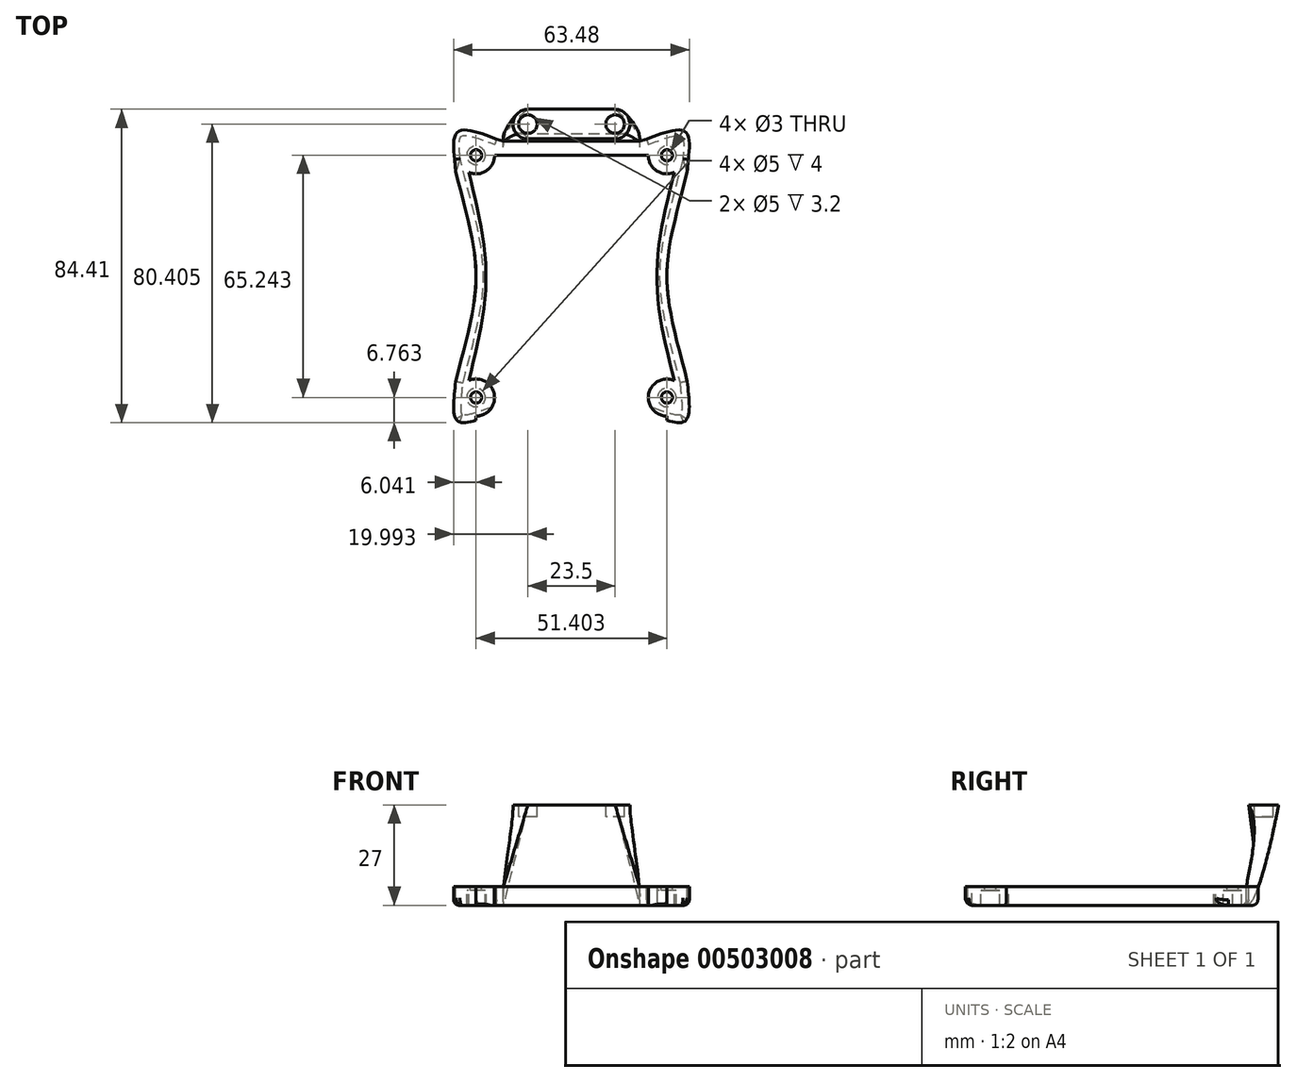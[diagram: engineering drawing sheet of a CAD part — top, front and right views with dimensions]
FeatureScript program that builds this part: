
annotation { "Feature Type Name" : "Feature", "Feature Type Description" : "" }
export const myFeature = defineFeature(function(context is Context, id is Id, definition is map)
    precondition{}
    {
        {
            var Q0;
            Q0=qCreatedBy(makeId("Top.planeOp"),FACE);
            var sketch = newSketch(context, id + "F0", { "sketchPlane" : qUnion([Q0])});
            skPoint(sketch, "E0.middle", {"position": v(-2.33, 0.15) * mm});
            skLineSegment(sketch, "E1.bottom", {"start": v(23.37, 32.78) * mm, "end": v(-28.03, 32.78) * mm, "construction": true});
            skLineSegment(sketch, "E1.top", {"start": v(23.37, -32.47) * mm, "end": v(-28.03, -32.47) * mm, "construction": true});
            skLineSegment(sketch, "E1.left", {"start": v(23.37, 32.78) * mm, "end": v(23.37, -32.47) * mm, "construction": true});
            skLineSegment(sketch, "E1.right", {"start": v(-28.03, 32.78) * mm, "end": v(-28.03, -32.47) * mm, "construction": true});
            skLineSegment(sketch, "E2.bottom", {"start": v(-67.33, 82.65) * mm, "end": v(62.67, 82.65) * mm, "construction": true});
            skLineSegment(sketch, "E2.top", {"start": v(-67.33, -82.35) * mm, "end": v(62.67, -82.35) * mm, "construction": true});
            skLineSegment(sketch, "E2.left", {"start": v(-67.33, 82.65) * mm, "end": v(-67.33, -82.35) * mm, "construction": true});
            skLineSegment(sketch, "E2.right", {"start": v(62.67, 82.65) * mm, "end": v(62.67, -82.35) * mm, "construction": true});
            skCircle(sketch, "E3", {"center": v(62.67, 82.65) * mm, "radius": 4.5 * mm, "construction": true});
            skCircle(sketch, "E4", {"center": v(-67.33, 82.65) * mm, "radius": 4.5 * mm, "construction": true});
            skCircle(sketch, "E5", {"center": v(62.67, -82.35) * mm, "radius": 4.5 * mm, "construction": true});
            skCircle(sketch, "E6", {"center": v(-67.33, -82.35) * mm, "radius": 4.5 * mm, "construction": true});
            skCircle(sketch, "E7", {"center": v(62.67, 82.65) * mm, "radius": 8 * mm, "construction": true});
            skCircle(sketch, "E8", {"center": v(62.67, -82.35) * mm, "radius": 8 * mm, "construction": true});
            skCircle(sketch, "E9", {"center": v(-67.33, -82.35) * mm, "radius": 8 * mm, "construction": true});
            skCircle(sketch, "E10", {"center": v(-67.33, 82.65) * mm, "radius": 8 * mm, "construction": true});
            skCircle(sketch, "E11", {"center": v(62.67, 82.65) * mm, "radius": 9.5 * mm, "construction": true});
            skCircle(sketch, "E12", {"center": v(62.67, -82.35) * mm, "radius": 9.5 * mm, "construction": true});
            skCircle(sketch, "E13", {"center": v(-67.33, -82.35) * mm, "radius": 9.5 * mm, "construction": true});
            skCircle(sketch, "E14", {"center": v(-67.33, 82.65) * mm, "radius": 9.5 * mm, "construction": true});
            skCircle(sketch, "E15", {"center": v(62.67, 82.65) * mm, "radius": 14 * mm, "construction": true});
            skCircle(sketch, "E16", {"center": v(-67.33, 82.65) * mm, "radius": 14 * mm, "construction": true});
            skCircle(sketch, "E17", {"center": v(62.67, -82.35) * mm, "radius": 14 * mm, "construction": true});
            skCircle(sketch, "E18", {"center": v(-67.33, -82.35) * mm, "radius": 14 * mm, "construction": true});
            skCircle(sketch, "E19", {"center": v(62.67, 82.65) * mm, "radius": 63.5 * mm, "construction": true});
            skCircle(sketch, "E20", {"center": v(62.67, -82.35) * mm, "radius": 63.5 * mm, "construction": true});
            skCircle(sketch, "E21", {"center": v(-67.33, -82.35) * mm, "radius": 63.5 * mm, "construction": true});
            skCircle(sketch, "E22", {"center": v(-67.33, 82.65) * mm, "radius": 63.5 * mm, "construction": true});
            skLineSegment(sketch, "E23.bottom", {"start": v(-28.52, 26.34) * mm, "end": v(23.86, 26.34) * mm, "construction": true});
            skLineSegment(sketch, "E23.top", {"start": v(-28.52, -26.04) * mm, "end": v(23.86, -26.04) * mm, "construction": true});
            skLineSegment(sketch, "E23.left", {"start": v(-28.52, 26.34) * mm, "end": v(-28.52, -26.04) * mm, "construction": true});
            skLineSegment(sketch, "E23.right", {"start": v(23.86, 26.34) * mm, "end": v(23.86, -26.04) * mm, "construction": true});
            skCircle(sketch, "E24", {"center": v(23.37, 32.78) * mm, "radius": 1.5 * mm, "construction": true});
            skCircle(sketch, "E25", {"center": v(-28.03, 32.78) * mm, "radius": 1.5 * mm, "construction": true});
            skCircle(sketch, "E26", {"center": v(23.37, -32.47) * mm, "radius": 1.5 * mm, "construction": true});
            skCircle(sketch, "E27", {"center": v(-28.03, -32.47) * mm, "radius": 1.5 * mm, "construction": true});
            skLineSegment(sketch, "E28", {"start": v(-67.33, 82.65) * mm, "end": v(62.67, -82.35) * mm, "construction": true});
            skLineSegment(sketch, "E29", {"start": v(62.67, 82.65) * mm, "end": v(-67.33, -82.35) * mm, "construction": true});
            skLineSegment(sketch, "E30.bottom", {"start": v(-17.58, -3.46) * mm, "end": v(12.92, -3.46) * mm, "construction": true});
            skLineSegment(sketch, "E30.top", {"start": v(-17.58, -33.96) * mm, "end": v(12.92, -33.96) * mm, "construction": true});
            skLineSegment(sketch, "E30.left", {"start": v(-17.58, -3.46) * mm, "end": v(-17.58, -33.96) * mm, "construction": true});
            skLineSegment(sketch, "E30.right", {"start": v(12.92, -3.46) * mm, "end": v(12.92, -33.96) * mm, "construction": true});
            skPoint(sketch, "E30.middle", {"position": v(-2.33, -18.71) * mm});
            skLineSegment(sketch, "E31.bottom", {"start": v(-17.58, 33.04) * mm, "end": v(12.92, 33.04) * mm, "construction": true});
            skLineSegment(sketch, "E31.top", {"start": v(-17.58, 2.54) * mm, "end": v(12.92, 2.54) * mm, "construction": true});
            skLineSegment(sketch, "E31.left", {"start": v(-17.58, 33.04) * mm, "end": v(-17.58, 2.54) * mm, "construction": true});
            skLineSegment(sketch, "E31.right", {"start": v(12.92, 33.04) * mm, "end": v(12.92, 2.54) * mm, "construction": true});
            skPoint(sketch, "E31.middle", {"position": v(-2.33, 17.79) * mm});
            skLineSegment(sketch, "E32", {"start": v(-2.33, 2.54) * mm, "end": v(-2.33, -3.46) * mm, "construction": true});
            skLineSegment(sketch, "E33", {"start": v(-2.33, 41.17) * mm, "end": v(-14.08, 41.17) * mm, "construction": true});
            skLineSegment(sketch, "E34", {"start": v(-2.33, 41.17) * mm, "end": v(9.42, 41.17) * mm, "construction": true});
            skLineSegment(sketch, "E35", {"start": v(-28.03, 32.78) * mm, "end": v(-22.53, 37.1) * mm, "construction": true});
            skLineSegment(sketch, "E36", {"start": v(-28.03, 32.78) * mm, "end": v(-33.53, 28.44) * mm, "construction": true});
            skLineSegment(sketch, "E37", {"start": v(-28.03, 32.78) * mm, "end": v(-32.98, 39.06) * mm, "construction": true});
            skLineSegment(sketch, "E38", {"start": v(23.37, 32.78) * mm, "end": v(28.33, 39.06) * mm, "construction": true});
            skLineSegment(sketch, "E39", {"start": v(23.37, 32.78) * mm, "end": v(17.88, 37.1) * mm, "construction": true});
            skLineSegment(sketch, "E40", {"start": v(23.37, 32.78) * mm, "end": v(28.87, 28.44) * mm, "construction": true});
            skLineSegment(sketch, "E41", {"start": v(23.37, -32.47) * mm, "end": v(28.33, -38.75) * mm, "construction": true});
            skLineSegment(sketch, "E42", {"start": v(23.37, -32.47) * mm, "end": v(17.88, -36.8) * mm, "construction": true});
            skLineSegment(sketch, "E43", {"start": v(23.37, -32.47) * mm, "end": v(28.87, -28.13) * mm, "construction": true});
            skLineSegment(sketch, "E44", {"start": v(-28.03, -32.47) * mm, "end": v(-32.98, -38.75) * mm, "construction": true});
            skLineSegment(sketch, "E45", {"start": v(-28.03, -32.47) * mm, "end": v(-22.53, -36.8) * mm, "construction": true});
            skLineSegment(sketch, "E46", {"start": v(-28.03, -32.47) * mm, "end": v(-33.53, -28.13) * mm, "construction": true});
            skFitSpline(sketch, "E47", {"points": [v(-22.53, 37.1) * mm, v(-32.98, 39.06) * mm, v(-33.53, 28.44) * mm], "startDerivative": vector(-20.3, 7.46) * mm, "endDerivative": vector(0.93, -21.61) * mm});
            skFitSpline(sketch, "E48", {"points": [v(17.88, 37.1) * mm, v(28.33, 39.06) * mm, v(28.87, 28.44) * mm], "startDerivative": vector(20.3, 7.46) * mm, "endDerivative": vector(-0.93, -21.61) * mm});
            skLineSegment(sketch, "E49", {"start": v(-14.08, 41.17) * mm, "end": v(-18.08, 41.17) * mm, "construction": true});
            skLineSegment(sketch, "E50", {"start": v(9.42, 41.17) * mm, "end": v(13.42, 41.17) * mm, "construction": true});
            skLineSegment(sketch, "E51", {"start": v(-2.33, 41.17) * mm, "end": v(-2.33, 45.17) * mm, "construction": true});
            skLineSegment(sketch, "E52", {"start": v(-18.08, 41.17) * mm, "end": v(-18.08, 41.17) * mm});
            skLineSegment(sketch, "E53", {"start": v(13.42, 41.17) * mm, "end": v(13.42, 41.17) * mm});
            skPoint(sketch, "E54.visualSharp", {"position": v(-18.08, 45.17) * mm});
            skPoint(sketch, "E55.visualSharp", {"position": v(13.42, 45.17) * mm});
            skLineSegment(sketch, "E56", {"start": v(-22.53, 37.1) * mm, "end": v(-20.66, 36.53) * mm});
            skPoint(sketch, "E57.visualSharp", {"position": v(-18.08, 35.74) * mm});
            skLineSegment(sketch, "E58", {"start": v(-18.08, 35.74) * mm, "end": v(-2.33, 35.74) * mm, "construction": true});
            skLineSegment(sketch, "E59", {"start": v(-2.33, 35.74) * mm, "end": v(13.42, 35.74) * mm, "construction": true});
            skLineSegment(sketch, "E60", {"start": v(17.88, 37.1) * mm, "end": v(16.01, 36.53) * mm});
            skPoint(sketch, "E61.visualSharp", {"position": v(13.42, 35.74) * mm});
            skCircle(sketch, "E62", {"center": v(-17.58, -33.96) * mm, "radius": 1.5 * mm});
            skCircle(sketch, "E63", {"center": v(12.92, -33.96) * mm, "radius": 1.5 * mm});
            skLineSegment(sketch, "E64", {"start": v(-2.33, -33.96) * mm, "end": v(-2.33, -37.96) * mm, "construction": true});
            skLineSegment(sketch, "E65", {"start": v(-17.58, -33.96) * mm, "end": v(-21.58, -33.96) * mm, "construction": true});
            skLineSegment(sketch, "E66", {"start": v(12.92, -33.96) * mm, "end": v(16.92, -33.96) * mm, "construction": true});
            skLineSegment(sketch, "E67", {"start": v(-21.58, -38.3) * mm, "end": v(-2.33, -38.3) * mm, "construction": true});
            skLineSegment(sketch, "E68", {"start": v(-2.33, -38.3) * mm, "end": v(16.92, -38.3) * mm, "construction": true});
            skPoint(sketch, "E69.visualSharp", {"position": v(-21.58, -38.3) * mm});
            skPoint(sketch, "E70.visualSharp", {"position": v(16.92, -38.3) * mm});
            skCircle(sketch, "E71", {"center": v(-12.13, -44.75) * mm, "radius": 1.5 * mm});
            skCircle(sketch, "E72", {"center": v(7.47, -44.75) * mm, "radius": 1.5 * mm});
            skLineSegment(sketch, "E73", {"start": v(-12.13, -44.75) * mm, "end": v(-2.33, -44.75) * mm, "construction": true});
            skLineSegment(sketch, "E74", {"start": v(-2.33, -44.75) * mm, "end": v(7.47, -44.75) * mm, "construction": true});
            skFitSpline(sketch, "E75", {"points": [v(-33.53, 28.44) * mm, v(-28.03, 0.15) * mm, v(-33.53, -28.13) * mm], "startDerivative": vector(16.96, -67.18) * mm, "endDerivative": vector(-16.96, -67.18) * mm});
            skFitSpline(sketch, "E76", {"points": [v(28.87, 28.44) * mm, v(23.37, 0.15) * mm, v(28.87, -28.13) * mm], "startDerivative": vector(-16.96, -67.18) * mm, "endDerivative": vector(16.96, -67.18) * mm});
            skLineSegment(sketch, "E77", {"start": v(-2.33, -44.75) * mm, "end": v(-2.33, -50.75) * mm, "construction": true});
            skLineSegment(sketch, "E78", {"start": v(-12.13, -44.75) * mm, "end": v(-16.13, -44.75) * mm, "construction": true});
            skLineSegment(sketch, "E79", {"start": v(-12.13, -44.75) * mm, "end": v(-12.13, -48.75) * mm, "construction": true});
            skLineSegment(sketch, "E80", {"start": v(7.47, -44.75) * mm, "end": v(11.47, -44.75) * mm, "construction": true});
            skLineSegment(sketch, "E81", {"start": v(7.47, -44.75) * mm, "end": v(7.47, -48.75) * mm, "construction": true});
            skCircle(sketch, "E82", {"center": v(-28.03, 32.78) * mm, "radius": 1.5 * mm});
            skCircle(sketch, "E83", {"center": v(23.37, 32.78) * mm, "radius": 1.5 * mm});
            skCircle(sketch, "E84", {"center": v(-28.03, -32.47) * mm, "radius": 1.5 * mm});
            skCircle(sketch, "E85", {"center": v(23.37, -32.47) * mm, "radius": 1.5 * mm});
            skLineSegment(sketch, "E86", {"start": v(-2.33, 32.78) * mm, "end": v(-2.33, 41.17) * mm, "construction": true});
            skLineSegment(sketch, "E87", {"start": v(115.22, -24.48) * mm, "end": v(115.22, 9.49) * mm, "construction": true});
            skLineSegment(sketch, "E88", {"start": v(-21.37, -36.36) * mm, "end": v(-2.33, -36.36) * mm, "construction": true});
            skLineSegment(sketch, "E89", {"start": v(-2.33, -36.36) * mm, "end": v(16.72, -36.36) * mm, "construction": true});
            skFitSpline(sketch, "E90", {"points": [v(-21.58, -38.3) * mm, v(-16.13, -44.75) * mm, v(-12.13, -48.75) * mm, v(-2.33, -50.75) * mm], "startDerivative": vector(17.01, -18.5) * mm, "endDerivative": vector(29.8, -3.11) * mm});
            skFitSpline(sketch, "E91", {"points": [v(16.92, -38.3) * mm, v(11.47, -44.75) * mm, v(7.47, -48.75) * mm, v(-2.33, -50.75) * mm], "startDerivative": vector(-17.98, -19.6) * mm, "endDerivative": vector(-29.8, -3.11) * mm});
            skLineSegment(sketch, "E92", {"start": v(116.25, 10.49) * mm, "end": v(169.47, 8.84) * mm, "construction": true});
            skPoint(sketch, "E93.visualSharp", {"position": v(115.22, 10.52) * mm});
            skArc(sketch, "E93.filletArc", {"start": v(116.25, 10.49) * mm, "mid": v(115.53, 10.2) * mm, "end": v(115.22, 9.49) * mm, "construction": true});
            skPoint(sketch, "E94.visualSharp", {"position": v(16.72, -36.36) * mm});
            skPoint(sketch, "E95.visualSharp", {"position": v(-21.37, -36.36) * mm});
            skLineSegment(sketch, "E96.bottom", {"start": v(-16.1, 17.65) * mm, "end": v(11.45, 17.65) * mm, "construction": true});
            skLineSegment(sketch, "E96.top", {"start": v(-16.1, -17.35) * mm, "end": v(11.45, -17.35) * mm, "construction": true});
            skLineSegment(sketch, "E96.left", {"start": v(-16.1, 17.65) * mm, "end": v(-16.1, -17.35) * mm, "construction": true});
            skLineSegment(sketch, "E96.right", {"start": v(11.45, 17.65) * mm, "end": v(11.45, -17.35) * mm, "construction": true});
            skLineSegment(sketch, "E97", {"start": v(-2.33, 13.23) * mm, "end": v(-20.53, 13.23) * mm, "construction": true});
            skLineSegment(sketch, "E98", {"start": v(-2.33, 13.23) * mm, "end": v(15.88, 13.23) * mm, "construction": true});
            skLineSegment(sketch, "E99", {"start": v(-2.33, 0.15) * mm, "end": v(-2.33, 14.42) * mm, "construction": true});
            skLineSegment(sketch, "E100", {"start": v(-2.33, 0.15) * mm, "end": v(14.67, 0.15) * mm, "construction": true});
            skLineSegment(sketch, "E101.bottom", {"start": v(-18.22, 14.7) * mm, "end": v(13.57, 14.7) * mm, "construction": true});
            skLineSegment(sketch, "E101.top", {"start": v(-18.22, -14.4) * mm, "end": v(13.57, -14.4) * mm, "construction": true});
            skLineSegment(sketch, "E101.left", {"start": v(-18.22, 14.7) * mm, "end": v(-18.22, -14.4) * mm, "construction": true});
            skLineSegment(sketch, "E101.right", {"start": v(13.57, 14.7) * mm, "end": v(13.57, -14.4) * mm, "construction": true});
            skLineSegment(sketch, "E102", {"start": v(-2.33, 26.07) * mm, "end": v(12, 26.07) * mm, "construction": true});
            skLineSegment(sketch, "E103", {"start": v(-2.33, 26.07) * mm, "end": v(-16.66, 26.07) * mm, "construction": true});
            skLineSegment(sketch, "E104.top", {"start": v(-17.4, 22.07) * mm, "end": v(-15.9, 22.07) * mm});
            skPoint(sketch, "E104.middle", {"position": v(-16.66, 26.07) * mm});
            skLineSegment(sketch, "E105.top", {"start": v(12.75, 22.07) * mm, "end": v(11.25, 22.07) * mm});
            skLineSegment(sketch, "E105.left", {"start": v(12.75, 30.07) * mm, "end": v(12.75, 22.07) * mm});
            skPoint(sketch, "E105.middle", {"position": v(12, 26.07) * mm});
            skFitSpline(sketch, "E106", {"points": [v(-33.53, -28.13) * mm, v(-32.98, -38.75) * mm, v(-22.93, -36.94) * mm], "startDerivative": vector(-1.92, -24.87) * mm, "endDerivative": vector(23.17, 7.34) * mm});
            skLineSegment(sketch, "E107", {"start": v(-22.93, -36.94) * mm, "end": v(-2.33, -36.94) * mm, "construction": true});
            skLineSegment(sketch, "E108", {"start": v(-2.33, -36.94) * mm, "end": v(18.28, -36.94) * mm, "construction": true});
            skLineSegment(sketch, "E109", {"start": v(16.92, -38.3) * mm, "end": v(17.66, -37.14) * mm});
            skLineSegment(sketch, "E110", {"start": v(18.25, -36.93) * mm, "end": v(18.28, -36.94) * mm});
            skLineSegment(sketch, "E111", {"start": v(-21.58, -38.3) * mm, "end": v(-22.32, -37.14) * mm});
            skLineSegment(sketch, "E112", {"start": v(-22.9, -36.93) * mm, "end": v(-22.93, -36.94) * mm});
            skLineSegment(sketch, "E113", {"start": v(169.47, 8.84) * mm, "end": v(169.47, -13.62) * mm, "construction": true});
            skPoint(sketch, "E114.visualSharp", {"position": v(17.88, -36.8) * mm});
            skArc(sketch, "E114.filletArc", {"start": v(18.25, -36.93) * mm, "mid": v(17.92, -36.93) * mm, "end": v(17.66, -37.14) * mm});
            skPoint(sketch, "E115.visualSharp", {"position": v(-22.53, -36.8) * mm});
            skArc(sketch, "E115.filletArc", {"start": v(-22.32, -37.14) * mm, "mid": v(-22.58, -36.93) * mm, "end": v(-22.9, -36.93) * mm});
            skLineSegment(sketch, "E116", {"start": v(-2.33, 0.15) * mm, "end": v(-2.33, 3.45) * mm, "construction": true});
            skLineSegment(sketch, "E117.bottom", {"start": v(-7.83, 5.65) * mm, "end": v(3.17, 5.65) * mm, "construction": true});
            skLineSegment(sketch, "E117.top", {"start": v(-7.83, -5.35) * mm, "end": v(3.17, -5.35) * mm, "construction": true});
            skLineSegment(sketch, "E117.left", {"start": v(-7.83, 5.65) * mm, "end": v(-7.83, -5.35) * mm, "construction": true});
            skLineSegment(sketch, "E117.right", {"start": v(3.17, 5.65) * mm, "end": v(3.17, -5.35) * mm, "construction": true});
            skLineSegment(sketch, "E118.bottom", {"start": v(-10.3, 10.77) * mm, "end": v(5.65, 10.77) * mm});
            skPoint(sketch, "E118.middle", {"position": v(-2.33, 12.75) * mm});
            skPoint(sketch, "E119.middle", {"position": v(-2.33, -26.45) * mm});
            skPoint(sketch, "E120", {"position": v(-2.33, -17.35) * mm});
            skPoint(sketch, "E121", {"position": v(-2.33, -26.04) * mm});
            skPoint(sketch, "E122.visualSharp", {"position": v(-2.33, 21.17) * mm});
            skArc(sketch, "E122.filletArc", {"start": v(-0.91, 19.76) * mm, "mid": v(-2.33, 20.34) * mm, "end": v(-3.74, 19.76) * mm});
            skPoint(sketch, "E123.visualSharp", {"position": v(-12.72, 10.77) * mm});
            skArc(sketch, "E123.filletArc", {"start": v(-11.02, 12.48) * mm, "mid": v(-11.23, 11.4) * mm, "end": v(-10.3, 10.77) * mm});
            skPoint(sketch, "E124.visualSharp", {"position": v(8.07, 10.77) * mm});
            skArc(sketch, "E124.filletArc", {"start": v(5.65, 10.77) * mm, "mid": v(6.58, 11.4) * mm, "end": v(6.36, 12.48) * mm});
            skPoint(sketch, "E125.visualSharp", {"position": v(-2.33, 0.75) * mm});
            skLineSegment(sketch, "E126", {"start": v(-1.33, 10.77) * mm, "end": v(-1.33, 6.27) * mm, "construction": true});
            skPoint(sketch, "E127.middle", {"position": v(-2.33, 9.75) * mm});
            skCircle(sketch, "E128", {"center": v(13.57, 14.7) * mm, "radius": 4.5 * mm, "construction": true});
            skCircle(sketch, "E129", {"center": v(-18.22, 14.7) * mm, "radius": 4.5 * mm, "construction": true});
            skCircle(sketch, "E130", {"center": v(13.57, -14.4) * mm, "radius": 4.5 * mm, "construction": true});
            skCircle(sketch, "E131", {"center": v(-18.22, -14.4) * mm, "radius": 4.5 * mm, "construction": true});
            skLineSegment(sketch, "E132", {"start": v(-2.33, 0.15) * mm, "end": v(-18.22, 14.7) * mm, "construction": true});
            skLineSegment(sketch, "E133", {"start": v(-2.33, 0.15) * mm, "end": v(13.57, 14.7) * mm, "construction": true});
            skLineSegment(sketch, "E134", {"start": v(13.57, 14.7) * mm, "end": v(23.37, 32.78) * mm, "construction": true});
            skLineSegment(sketch, "E135", {"start": v(-18.22, 14.7) * mm, "end": v(-28.03, 32.78) * mm, "construction": true});
            skLineSegment(sketch, "E136", {"start": v(-2.33, 0.15) * mm, "end": v(-18.22, -14.4) * mm, "construction": true});
            skLineSegment(sketch, "E137", {"start": v(-18.22, -14.4) * mm, "end": v(-28.03, -32.47) * mm, "construction": true});
            skLineSegment(sketch, "E138", {"start": v(-2.33, 0.15) * mm, "end": v(13.57, -14.4) * mm, "construction": true});
            skLineSegment(sketch, "E139", {"start": v(13.57, -14.4) * mm, "end": v(23.37, -32.47) * mm, "construction": true});
            skPoint(sketch, "E140.visualSharp", {"position": v(-4.57, 37.81) * mm});
            skPoint(sketch, "E141.visualSharp", {"position": v(-12.93, 29.46) * mm});
            skPoint(sketch, "E142.visualSharp", {"position": v(-4.57, 26.22) * mm});
            skArc(sketch, "E142.filletArc", {"start": v(-5.16, 25.63) * mm, "mid": v(-4.73, 26.28) * mm, "end": v(-4.57, 27.04) * mm});
            skPoint(sketch, "E143.visualSharp", {"position": v(-0.08, 26.22) * mm});
            skPoint(sketch, "E144.visualSharp", {"position": v(-0.08, 37.81) * mm});
            skPoint(sketch, "E145.visualSharp", {"position": v(8.28, 17.86) * mm});
            skPoint(sketch, "E146.visualSharp", {"position": v(-12.93, 17.86) * mm});
            skLineSegment(sketch, "E147", {"start": v(-2.33, -22.87) * mm, "end": v(-10.31, -22.87) * mm});
            skLineSegment(sketch, "E148", {"start": v(-2.33, -22.87) * mm, "end": v(5.66, -22.87) * mm});
            skPoint(sketch, "E149.visualSharp", {"position": v(8.07, -22.87) * mm});
            skArc(sketch, "E149.filletArc", {"start": v(6.37, -24.57) * mm, "mid": v(6.58, -23.48) * mm, "end": v(5.66, -22.87) * mm});
            skPoint(sketch, "E150.visualSharp", {"position": v(-12.73, -22.87) * mm});
            skArc(sketch, "E150.filletArc", {"start": v(-10.31, -22.87) * mm, "mid": v(-11.24, -23.48) * mm, "end": v(-11.02, -24.57) * mm});
            skPoint(sketch, "E151.visualSharp", {"position": v(-2.33, -33.27) * mm});
            skArc(sketch, "E151.filletArc", {"start": v(-3.74, -31.85) * mm, "mid": v(-2.33, -32.44) * mm, "end": v(-0.91, -31.85) * mm});
            skFitSpline(sketch, "E152", {"points": [v(28.87, -28.13) * mm, v(28.33, -38.75) * mm, v(18.28, -36.94) * mm], "startDerivative": vector(1.93, -24.89) * mm, "endDerivative": vector(-23.2, 7.39) * mm});
            skLineSegment(sketch, "E153", {"start": v(-5.66, -36.7) * mm, "end": v(-5.66, -42.34) * mm});
            skLineSegment(sketch, "E154", {"start": v(-12.73, -36.85) * mm, "end": v(-12.73, -31.22) * mm});
            skLineSegment(sketch, "E155", {"start": v(1, -36.7) * mm, "end": v(1, -42.34) * mm});
            skLineSegment(sketch, "E156", {"start": v(8.07, -36.85) * mm, "end": v(8.07, -31.22) * mm});
            skPoint(sketch, "E157.visualSharp", {"position": v(8.07, -28.8) * mm});
            skArc(sketch, "E157.filletArc", {"start": v(8.07, -31.22) * mm, "mid": v(7.46, -30.3) * mm, "end": v(6.37, -30.5) * mm});
            skPoint(sketch, "E158.visualSharp", {"position": v(1, -44.75) * mm});
            skArc(sketch, "E158.filletArc", {"start": v(1, -42.34) * mm, "mid": v(1.62, -43.26) * mm, "end": v(2.7, -43.05) * mm});
            skPoint(sketch, "E159.visualSharp", {"position": v(-5.66, -44.75) * mm});
            skArc(sketch, "E159.filletArc", {"start": v(-7.36, -43.05) * mm, "mid": v(-6.27, -43.26) * mm, "end": v(-5.66, -42.34) * mm});
            skPoint(sketch, "E160.visualSharp", {"position": v(-12.73, -28.8) * mm});
            skArc(sketch, "E160.filletArc", {"start": v(-11.02, -30.5) * mm, "mid": v(-12.1, -30.3) * mm, "end": v(-12.73, -31.22) * mm});
            skPoint(sketch, "E161.visualSharp", {"position": v(-5.66, -35.87) * mm});
            skArc(sketch, "E161.filletArc", {"start": v(-5.66, -36.7) * mm, "mid": v(-5.8, -35.94) * mm, "end": v(-6.24, -35.29) * mm});
            skPoint(sketch, "E162.visualSharp", {"position": v(-12.73, -37.68) * mm});
            skArc(sketch, "E162.filletArc", {"start": v(-12.73, -36.85) * mm, "mid": v(-12.57, -37.62) * mm, "end": v(-12.14, -38.27) * mm});
            skPoint(sketch, "E163.visualSharp", {"position": v(1, -35.87) * mm});
            skArc(sketch, "E163.filletArc", {"start": v(1.59, -35.29) * mm, "mid": v(1.15, -35.94) * mm, "end": v(1, -36.7) * mm});
            skPoint(sketch, "E164.visualSharp", {"position": v(8.07, -37.68) * mm});
            skArc(sketch, "E164.filletArc", {"start": v(7.49, -38.27) * mm, "mid": v(7.92, -37.62) * mm, "end": v(8.07, -36.85) * mm});
            skLineSegment(sketch, "E165", {"start": v(-2.33, -18.71) * mm, "end": v(-10.31, -18.71) * mm});
            skLineSegment(sketch, "E166", {"start": v(-2.33, -18.71) * mm, "end": v(5.66, -18.71) * mm});
            skPoint(sketch, "E167.visualSharp", {"position": v(-2.33, -8.31) * mm});
            skArc(sketch, "E167.filletArc", {"start": v(-0.91, -9.72) * mm, "mid": v(-2.33, -9.14) * mm, "end": v(-3.74, -9.72) * mm});
            skPoint(sketch, "E168.visualSharp", {"position": v(-12.73, -18.71) * mm});
            skArc(sketch, "E168.filletArc", {"start": v(-11.02, -17) * mm, "mid": v(-11.24, -18.1) * mm, "end": v(-10.31, -18.71) * mm});
            skPoint(sketch, "E169.visualSharp", {"position": v(8.07, -18.71) * mm});
            skArc(sketch, "E169.filletArc", {"start": v(5.66, -18.71) * mm, "mid": v(6.58, -18.1) * mm, "end": v(6.37, -17) * mm});
            skLineSegment(sketch, "E170", {"start": v(14.67, 0.15) * mm, "end": v(17.67, 0.15) * mm, "construction": true});
            skCircle(sketch, "E171", {"center": v(23.37, 32.78) * mm, "radius": 7 * mm, "construction": true});
            skLineSegment(sketch, "E172", {"start": v(17.64, 12.88) * mm, "end": v(21.69, 20.22) * mm});
            skLineSegment(sketch, "E173", {"start": v(16.8, 5.92) * mm, "end": v(12.23, 5.92) * mm});
            skPoint(sketch, "E174.visualSharp", {"position": v(22.7, 22.04) * mm});
            skArc(sketch, "E174.filletArc", {"start": v(22.15, 20.04) * mm, "mid": v(22, 20.33) * mm, "end": v(21.69, 20.22) * mm});
            skPoint(sketch, "E175.visualSharp", {"position": v(18.33, 5.92) * mm});
            skArc(sketch, "E175.filletArc", {"start": v(16.8, 5.92) * mm, "mid": v(18.02, 6.34) * mm, "end": v(18.73, 7.4) * mm});
            skPoint(sketch, "E176.visualSharp", {"position": v(9.29, 5.92) * mm});
            skArc(sketch, "E176.filletArc", {"start": v(11.62, 7.72) * mm, "mid": v(11.28, 6.6) * mm, "end": v(12.23, 5.92) * mm});
            skPoint(sketch, "E177.visualSharp", {"position": v(17.14, 11.97) * mm});
            skArc(sketch, "E177.filletArc", {"start": v(16.31, 11.33) * mm, "mid": v(17.06, 12.04) * mm, "end": v(17.64, 12.88) * mm});
            skLineSegment(sketch, "E178", {"start": v(9.29, 5.92) * mm, "end": v(-2.33, 5.92) * mm, "construction": true});
            skPoint(sketch, "E178.endSnap0", {"position": v(-2.33, 5.65) * mm});
            skLineSegment(sketch, "E179", {"start": v(-2.33, 5.92) * mm, "end": v(-13.94, 5.92) * mm, "construction": true});
            skLineSegment(sketch, "E180", {"start": v(-16.88, 5.92) * mm, "end": v(-21.46, 5.92) * mm});
            skLineSegment(sketch, "E181", {"start": v(17.14, 11.97) * mm, "end": v(-2.33, 11.97) * mm, "construction": true});
            skLineSegment(sketch, "E182", {"start": v(-2.33, 11.97) * mm, "end": v(-21.8, 11.97) * mm, "construction": true});
            skLineSegment(sketch, "E183", {"start": v(22.7, 22.04) * mm, "end": v(-2.33, 22.04) * mm, "construction": true});
            skLineSegment(sketch, "E184", {"start": v(-2.33, 22.04) * mm, "end": v(-27.34, 22.04) * mm, "construction": true});
            skLineSegment(sketch, "E185", {"start": v(-22.3, 12.88) * mm, "end": v(-26.34, 20.22) * mm});
            skPoint(sketch, "E186.visualSharp", {"position": v(-27.34, 22.04) * mm});
            skArc(sketch, "E186.filletArc", {"start": v(-26.34, 20.22) * mm, "mid": v(-26.65, 20.33) * mm, "end": v(-26.8, 20.04) * mm});
            skPoint(sketch, "E187.visualSharp", {"position": v(-13.94, 5.92) * mm});
            skArc(sketch, "E187.filletArc", {"start": v(-16.88, 5.92) * mm, "mid": v(-15.93, 6.6) * mm, "end": v(-16.27, 7.72) * mm});
            skPoint(sketch, "E188.visualSharp", {"position": v(-22.99, 5.92) * mm});
            skArc(sketch, "E188.filletArc", {"start": v(-23.39, 7.4) * mm, "mid": v(-22.67, 6.34) * mm, "end": v(-21.46, 5.92) * mm});
            skPoint(sketch, "E189.visualSharp", {"position": v(-21.8, 11.97) * mm});
            skArc(sketch, "E189.filletArc", {"start": v(-22.3, 12.88) * mm, "mid": v(-21.71, 12.04) * mm, "end": v(-20.97, 11.33) * mm});
            skLineSegment(sketch, "E190", {"start": v(-2.33, 43.17) * mm, "end": v(0, 43.17) * mm, "construction": true});
            skLineSegment(sketch, "E191", {"start": v(-20.66, 36.53) * mm, "end": v(16.01, 36.53) * mm});
            skSolve(sketch);
        }
        {
            var Q0;
            Q0=qCreatedBy(makeId("Top.planeOp"),FACE);
            cPlane(context, id + "F1", {"entities" : qUnion([Q0]), "cplaneType" : CPlaneType.OFFSET, "offset" : 22 * mm, "width" : 150 * mm, "height" : 150 * mm});
        }
        {
            var Q0;
            Q0=qCreatedBy(id+"F1.planeOp",FACE);
            var sketch = newSketch(context, id + "F2", { "sketchPlane" : qUnion([Q0])});
            skCircle(sketch, "E192", {"center": v(-14.08, 41.18) * mm, "radius": 4 * mm, "construction": true});
            skCircle(sketch, "E193", {"center": v(9.42, 41.18) * mm, "radius": 4 * mm, "construction": true});
            skLineSegment(sketch, "E194", {"start": v(-14.08, 41.18) * mm, "end": v(-14.08, 45.18) * mm, "construction": true});
            skLineSegment(sketch, "E195", {"start": v(-14.08, 41.18) * mm, "end": v(-18.08, 41.18) * mm, "construction": true});
            skLineSegment(sketch, "E196", {"start": v(9.42, 41.18) * mm, "end": v(9.42, 45.18) * mm, "construction": true});
            skLineSegment(sketch, "E197", {"start": v(9.42, 41.18) * mm, "end": v(13.42, 41.18) * mm, "construction": true});
            skArc(sketch, "E198", {"start": v(-14.08, 45.18) * mm, "mid": v(-16.9, 44) * mm, "end": v(-18.08, 41.18) * mm});
            skArc(sketch, "E199", {"start": v(13.42, 41.18) * mm, "mid": v(12.25, 44) * mm, "end": v(9.42, 45.18) * mm});
            skLineSegment(sketch, "E200", {"start": v(-14.08, 45.18) * mm, "end": v(9.42, 45.18) * mm});
            skLineSegment(sketch, "E201", {"start": v(-14.08, 41.18) * mm, "end": v(-14.08, 37.18) * mm, "construction": true});
            skLineSegment(sketch, "E202", {"start": v(9.42, 41.18) * mm, "end": v(9.42, 37.18) * mm, "construction": true});
            skArc(sketch, "E203", {"start": v(-18.08, 41.18) * mm, "mid": v(-16.9, 38.35) * mm, "end": v(-14.08, 37.18) * mm});
            skArc(sketch, "E204", {"start": v(9.42, 37.18) * mm, "mid": v(12.25, 38.35) * mm, "end": v(13.42, 41.18) * mm});
            skLineSegment(sketch, "E205", {"start": v(9.42, 37.18) * mm, "end": v(-14.08, 37.18) * mm});
            skLineSegment(sketch, "E206", {"start": v(-2.33, 37.18) * mm, "end": v(-2.33, 40.68) * mm, "construction": true});
            skLineSegment(sketch, "E207", {"start": v(-2.33, 40.68) * mm, "end": v(0, 40.68) * mm, "construction": true});
            skSolve(sketch);
        }
        {
            var Q0;
            Q0=qSketchRegion(id+"F0",true);
            extrude(context, id + "F3", {"entities" : qUnion([Q0]), "oppositeDirection" : true, "depth" : 5 * mm});
        }
        {
            var Q0;
            Q0=sQuery(id+"F2.wireOp",VERTEX,"E200.start");
            var Q1;
            Q1=sQuery(id+"F2.wireOp",VERTEX,"E201.end");
            var Q2;
            Q2=makeQuery(id+"F3.opExtrude","CAP_VERTEX",VERTEX,{"disambiguationData":[OSD([sQuery(id+"F0.wireOp",EDGE,"E56"),sQuery(id+"F0.wireOp",EDGE,"E191")])],"isStart":true});
            cPlane(context, id + "F4", {"entities" : qUnion([Q0, Q1, Q2]), "cplaneType" : CPlaneType.THREE_POINT, "offset" : 25 * mm, "width" : 150 * mm, "height" : 150 * mm});
        }
        {
            var Q0;
            Q0=sQuery(id+"F2.wireOp",VERTEX,"E199.end");
            var Q1;
            Q1=sQuery(id+"F2.wireOp",VERTEX,"E205.start");
            var Q2;
            Q2=makeQuery(id+"F3.opExtrude","CAP_VERTEX",VERTEX,{"disambiguationData":[OSD([sQuery(id+"F0.wireOp",EDGE,"E60"),sQuery(id+"F0.wireOp",EDGE,"E191")])],"isStart":true});
            cPlane(context, id + "F5", {"entities" : qUnion([Q0, Q1, Q2]), "cplaneType" : CPlaneType.THREE_POINT, "offset" : 25 * mm, "width" : 150 * mm, "height" : 150 * mm});
        }
        {
            var Q0;
            Q0=qCreatedBy(id+"F4.planeOp",FACE);
            var sketch = newSketch(context, id + "F6", { "sketchPlane" : qUnion([Q0])});
            skFitSpline(sketch, "E208", {"points": [v(-37.18, 17.04) * mm, v(-36.53, -5.93) * mm], "startDerivative": vector(-8.46, -14.5) * mm, "endDerivative": vector(4.23, -21.62) * mm});
            skSolve(sketch);
        }
        {
            var Q0;
            Q0=sQuery(id+"F2.wireOp",VERTEX,"E200.start");
            var Q1;
            Q1=sQuery(id+"F6.wireOp",VERTEX,"E208.start");
            var Q2;
            Q2=makeQuery(id+"F3.opExtrude","CAP_VERTEX",VERTEX,{"disambiguationData":[OSD([sQuery(id+"F0.wireOp",EDGE,"E56"),sQuery(id+"F0.wireOp",EDGE,"E191")])],"isStart":false});
            cPlane(context, id + "F7", {"entities" : qUnion([Q0, Q1, Q2]), "cplaneType" : CPlaneType.THREE_POINT, "offset" : 25 * mm, "width" : 150 * mm, "height" : 150 * mm});
        }
        {
            var Q0;
            Q0=qCreatedBy(id+"F7.planeOp",FACE);
            var sketch = newSketch(context, id + "F8", { "sketchPlane" : qUnion([Q0])});
            skFitSpline(sketch, "E209", {"points": [v(-45.18, 18.04) * mm, v(-36.53, -9.76) * mm], "startDerivative": vector(1.94, -10.2) * mm, "endDerivative": vector(10.23, -0.3) * mm});
            skSolve(sketch);
        }
        {
            var Q0;
            Q0=qCreatedBy(id+"F5.planeOp",FACE);
            var sketch = newSketch(context, id + "F9", { "sketchPlane" : qUnion([Q0])});
            skFitSpline(sketch, "E210", {"points": [v(-37.18, 18.37) * mm, v(-36.53, -4.6) * mm], "startDerivative": vector(-9.48, -17.55) * mm, "endDerivative": vector(2.7, -19.83) * mm});
            skSolve(sketch);
        }
        {
            var Q0;
            Q0=sQuery(id+"F2.wireOp",VERTEX,"E199.end");
            var Q1;
            Q1=sQuery(id+"F9.wireOp",VERTEX,"E210.start");
            var Q2;
            Q2=makeQuery(id+"F3.opExtrude","CAP_VERTEX",VERTEX,{"disambiguationData":[OSD([sQuery(id+"F0.wireOp",EDGE,"E60"),sQuery(id+"F0.wireOp",EDGE,"E191")])],"isStart":false});
            cPlane(context, id + "F10", {"entities" : qUnion([Q0, Q1, Q2]), "cplaneType" : CPlaneType.THREE_POINT, "offset" : 25 * mm, "width" : 150 * mm, "height" : 150 * mm});
        }
        {
            var Q0;
            Q0=qCreatedBy(id+"F10.planeOp",FACE);
            var sketch = newSketch(context, id + "F11", { "sketchPlane" : qUnion([Q0])});
            skFitSpline(sketch, "E211", {"points": [v(-45.18, 19.14) * mm, v(-36.53, -8.65) * mm], "startDerivative": vector(1.66, -8.07) * mm, "endDerivative": vector(10.78, -0.87) * mm});
            skSolve(sketch);
        }
        {
            var Q1;
            Q1=makeQuery(id+"F2.imprint","IMPRINT",FACE,{"disambiguationData":[TD([[makeQuery(id+"F2.imprint","IMPRINT",EDGE,{"derivedFrom":sQuery(id+"F2.wireOp",EDGE,"E198")}),1.0]])]});
            var Q2;
            Q2=makeQuery(id+"F3.opExtrude","SWEPT_FACE",FACE,{"disambiguationData":[OSD([sQuery(id+"F0.wireOp",EDGE,"E191")])]});
            var Q3;
            Q3=sQuery(id+"F11.wireOp",EDGE,"E211");
            var Q4;
            Q4=sQuery(id+"F8.wireOp",EDGE,"E209");
            var Q5;
            Q5=sQuery(id+"F9.wireOp",EDGE,"E210");
            var Q6;
            Q6=sQuery(id+"F6.wireOp",EDGE,"E208");
            loft(context, id + "F12", {"operationType" : NewBodyOperationType.ADD, "addGuides" : true, "sheetProfilesArray" : [{ "sheetProfileEntities" : qUnion([Q1]) }, { "sheetProfileEntities" : qUnion([Q2]) }], "guidesArray" : [{ "guideEntities" : qUnion([Q3]), "guideDerivativeType" : LoftGuideDerivativeType.DEFAULT, "guideDerivativeMagnitude" : 1 }, { "guideEntities" : qUnion([Q4]), "guideDerivativeType" : LoftGuideDerivativeType.DEFAULT, "guideDerivativeMagnitude" : 1 }, { "guideEntities" : qUnion([Q5]), "guideDerivativeType" : LoftGuideDerivativeType.DEFAULT, "guideDerivativeMagnitude" : 1 }, { "guideEntities" : qUnion([Q6]), "guideDerivativeType" : LoftGuideDerivativeType.DEFAULT, "guideDerivativeMagnitude" : 1 }]});
        }
        {
            var Q0;
            Q0=qCreatedBy(makeId("Top.planeOp"),FACE);
            var sketch = newSketch(context, id + "F13", { "sketchPlane" : qUnion([Q0])});
            skLineSegment(sketch, "E212", {"start": v(0, 15.53) * mm, "end": v(-2.33, 15.53) * mm, "construction": true});
            skLineSegment(sketch, "E213", {"start": v(-2.33, 34.2) * mm, "end": v(-2.33, -48.18) * mm, "construction": true});
            skCircle(sketch, "E214", {"center": v(-28.03, 32.78) * mm, "radius": 5 * mm, "construction": true});
            skCircle(sketch, "E215", {"center": v(23.37, 32.78) * mm, "radius": 5 * mm, "construction": true});
            skLineSegment(sketch, "E216", {"start": v(-23.03, 32.78) * mm, "end": v(18.37, 32.78) * mm});
            skArc(sketch, "E217", {"start": v(-28.03, 27.78) * mm, "mid": v(-24.5, 29.24) * mm, "end": v(-23.03, 32.78) * mm});
            skArc(sketch, "E218", {"start": v(18.37, 32.78) * mm, "mid": v(19.84, 29.24) * mm, "end": v(23.37, 27.78) * mm});
            skCircle(sketch, "E219", {"center": v(-28.03, -32.47) * mm, "radius": 5 * mm, "construction": true});
            skCircle(sketch, "E220", {"center": v(23.37, -32.47) * mm, "radius": 5 * mm, "construction": true});
            skLineSegment(sketch, "E221", {"start": v(23.37, -37.47) * mm, "end": v(23.37, -52.19) * mm});
            skLineSegment(sketch, "E222", {"start": v(-2.33, 0) * mm, "end": v(-25.33, 0) * mm, "construction": true});
            skLineSegment(sketch, "E223", {"start": v(-2.33, 0) * mm, "end": v(20.67, 0) * mm, "construction": true});
            skArc(sketch, "E224", {"start": v(23.37, -27.47) * mm, "mid": v(18.37, -32.47) * mm, "end": v(23.37, -37.47) * mm});
            skLineSegment(sketch, "E225", {"start": v(-28.03, -37.47) * mm, "end": v(-28.03, -52.19) * mm});
            skLineSegment(sketch, "E226", {"start": v(-28.03, -52.19) * mm, "end": v(23.37, -52.19) * mm});
            skArc(sketch, "E227", {"start": v(-28.03, -37.47) * mm, "mid": v(-23.06, -32.47) * mm, "end": v(-28.03, -27.47) * mm});
            skLineSegment(sketch, "E228", {"start": v(-23.03, 32.78) * mm, "end": v(-30, 32.78) * mm, "construction": true});
            skLineSegment(sketch, "E229", {"start": v(18.37, 32.78) * mm, "end": v(25.35, 32.78) * mm, "construction": true});
            skLineSegment(sketch, "E230", {"start": v(-23.06, -32.47) * mm, "end": v(-30.03, -32.47) * mm, "construction": true});
            skLineSegment(sketch, "E231", {"start": v(18.37, -32.47) * mm, "end": v(25.35, -32.47) * mm, "construction": true});
            skPoint(sketch, "E231.startSnap0", {"position": v(18.37, -32.47) * mm});
            skFitSpline(sketch, "E232", {"points": [v(-30, 28.18) * mm, v(-25.33, 0) * mm, v(-30, -27.87) * mm], "startDerivative": vector(14.01, -56.3) * mm, "endDerivative": vector(-14.04, -55.82) * mm});
            skFitSpline(sketch, "E233", {"points": [v(25.35, 28.18) * mm, v(20.67, 0) * mm, v(25.35, -27.87) * mm], "startDerivative": vector(-14.01, -56.3) * mm, "endDerivative": vector(14.04, -55.82) * mm});
            skArc(sketch, "E234", {"start": v(-28.03, -27.47) * mm, "mid": v(-29.04, -27.57) * mm, "end": v(-30, -27.87) * mm});
            skArc(sketch, "E235", {"start": v(25.35, -27.87) * mm, "mid": v(24.38, -27.57) * mm, "end": v(23.37, -27.47) * mm});
            skArc(sketch, "E236", {"start": v(-30, 28.18) * mm, "mid": v(-29.04, 27.88) * mm, "end": v(-28.03, 27.78) * mm});
            skArc(sketch, "E237", {"start": v(23.37, 27.78) * mm, "mid": v(24.38, 27.88) * mm, "end": v(25.35, 28.18) * mm});
            skSolve(sketch);
        }
        {
            var Q0;
            Q0=qSketchRegion(id+"F13",true);
            extrude(context, id + "F14", {"entities" : qUnion([Q0]), "operationType" : NewBodyOperationType.REMOVE, "oppositeDirection" : true, "depth" : 5 * mm});
        }
        {
            var Q0;
            Q0=makeQuery(id+"F3.opExtrude","CAP_EDGE",EDGE,{"disambiguationData":[OSD([sQuery(id+"F0.wireOp",EDGE,"E75")])],"isStart":false});
            var Q1;
            Q1=makeQuery(id+"F3.opExtrude","CAP_EDGE",EDGE,{"disambiguationData":[OSD([sQuery(id+"F0.wireOp",EDGE,"E76")])],"isStart":false});
            var Q2;
            Q2=makeQuery(id+"F14.boolean.opBoolean","COPY",EDGE,{"derivedFrom":makeQuery(id+"F14.opExtrude","CAP_EDGE",EDGE,{"disambiguationData":[OSD([sQuery(id+"F13.wireOp",EDGE,"3efa2638-28cb-410d-a451-7c4a5f4f91e7")])],"isStart":false})});
            var Q3;
            Q3=makeQuery(id+"F14.boolean.opBoolean","COPY",EDGE,{"derivedFrom":makeQuery(id+"F14.opExtrude","CAP_EDGE",EDGE,{"disambiguationData":[OSD([sQuery(id+"F13.wireOp",EDGE,"fab21a03-1c0a-4784-8c2c-017c8e7d5961")])],"isStart":false})});
            var Q4;
            Q4=makeQuery(id+"F3.opExtrude","CAP_EDGE",EDGE,{"disambiguationData":[OSD([sQuery(id+"F0.wireOp",EDGE,"E152")])],"isStart":false});
            var Q5;
            Q5=makeQuery(id+"F3.opExtrude","CAP_EDGE",EDGE,{"disambiguationData":[OSD([sQuery(id+"F0.wireOp",EDGE,"E106")])],"isStart":false});
            fillet(context, id + "F15", {"entities" : qUnion([Q0, Q1, Q2, Q3, Q4, Q5]), "radius" : 2 * mm, "tangentPropagation" : true, "allowEdgeOverflow" : false});
        }
        {
            var Q0;
            Q0=makeQuery(id+"F3.opExtrude","CAP_EDGE",EDGE,{"disambiguationData":[OSD([sQuery(id+"F0.wireOp",EDGE,"E47")])],"isStart":false});
            var Q1;
            Q1=makeQuery(id+"F3.opExtrude","CAP_EDGE",EDGE,{"disambiguationData":[OSD([sQuery(id+"F0.wireOp",EDGE,"E48")])],"isStart":false});
            fillet(context, id + "F16", {"entities" : qUnion([Q0, Q1]), "radius" : 1.5 * mm, "tangentPropagation" : true, "allowEdgeOverflow" : false});
        }
        {
            var Q0;
            Q0=qCreatedBy(makeId("Top.planeOp"),FACE);
            var sketch = newSketch(context, id + "F17", { "sketchPlane" : qUnion([Q0])});
            skCircle(sketch, "E238", {"center": v(-28.03, 32.78) * mm, "radius": 2.5 * mm});
            skCircle(sketch, "E239", {"center": v(23.37, 32.78) * mm, "radius": 2.5 * mm});
            skCircle(sketch, "E240", {"center": v(23.37, -32.47) * mm, "radius": 2.5 * mm});
            skCircle(sketch, "E241", {"center": v(-28.03, -32.47) * mm, "radius": 2.5 * mm});
            skSolve(sketch);
        }
        {
            var Q0;
            Q0=qSketchRegion(id+"F17",true);
            extrude(context, id + "F18", {"entities" : qUnion([Q0]), "operationType" : NewBodyOperationType.REMOVE, "oppositeDirection" : true, "depth" : 5 * mm, "hasSecondDirection" : true, "secondDirectionOppositeDirection" : true, "secondDirectionDepth" : 1 * mm});
        }
        {
            var Q0;
            Q0=qCreatedBy(id+"F1.planeOp",FACE);
            var sketch = newSketch(context, id + "F19", { "sketchPlane" : qUnion([Q0])});
            skCircle(sketch, "E242", {"center": v(-14.08, 41.18) * mm, "radius": 1.5 * mm});
            skCircle(sketch, "E243", {"center": v(9.42, 41.18) * mm, "radius": 1.5 * mm});
            skCircle(sketch, "E244", {"center": v(-14.08, 41.18) * mm, "radius": 2.5 * mm});
            skCircle(sketch, "E245", {"center": v(9.42, 41.18) * mm, "radius": 2.5 * mm});
            skSolve(sketch);
        }
        {
            var Q0;
            Q0=qCreatedBy(id+"F1.planeOp",FACE);
            var sketch = newSketch(context, id + "F20", { "sketchPlane" : qUnion([Q0])});
            skArc(sketch, "E246", {"start": v(-16.58, 41.18) * mm, "mid": v(-14.08, 38.68) * mm, "end": v(-11.58, 41.18) * mm});
            skArc(sketch, "E247", {"start": v(6.92, 41.18) * mm, "mid": v(9.42, 38.68) * mm, "end": v(11.92, 41.18) * mm});
            skLineSegment(sketch, "E248", {"start": v(-16.58, 41.18) * mm, "end": v(-16.58, 45.78) * mm});
            skLineSegment(sketch, "E249", {"start": v(-11.58, 41.18) * mm, "end": v(-11.58, 45.78) * mm});
            skLineSegment(sketch, "E250", {"start": v(-11.58, 45.78) * mm, "end": v(-16.58, 45.78) * mm});
            skLineSegment(sketch, "E251", {"start": v(6.92, 41.18) * mm, "end": v(6.92, 46.07) * mm});
            skLineSegment(sketch, "E252", {"start": v(11.92, 41.18) * mm, "end": v(11.92, 46.07) * mm});
            skLineSegment(sketch, "E253", {"start": v(11.92, 46.07) * mm, "end": v(6.92, 46.07) * mm});
            skSolve(sketch);
        }
        {
            var Q0;
            Q0=qCreatedBy(id+"F1.planeOp",FACE);
            var sketch = newSketch(context, id + "F21", { "sketchPlane" : qUnion([Q0])});
            skCircle(sketch, "E254", {"center": v(-14.08, 41.18) * mm, "radius": 2.5 * mm});
            skCircle(sketch, "E255", {"center": v(9.42, 41.18) * mm, "radius": 2.5 * mm});
            skSolve(sketch);
        }
        {
            var Q0;
            Q0=qSketchRegion(id+"F21",true);
            extrude(context, id + "F22", {"entities" : qUnion([Q0]), "operationType" : NewBodyOperationType.REMOVE, "oppositeDirection" : true, "depth" : 3.2 * mm});
        }
    });
